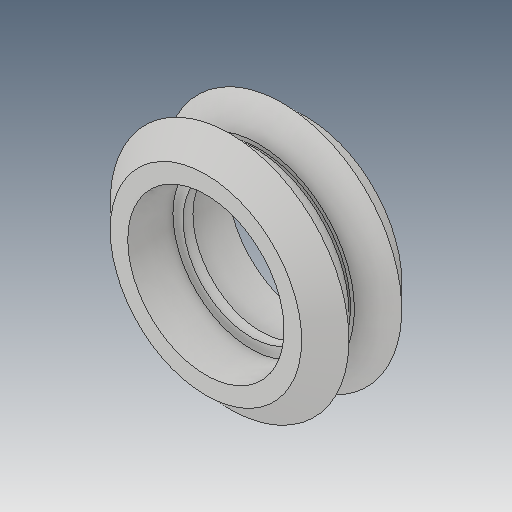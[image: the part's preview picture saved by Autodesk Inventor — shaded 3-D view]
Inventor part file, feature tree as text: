
AUTODESK INVENTOR PART (.ipt)
format: ipt  version: 2017 (Build 210142000, 142)  size: 159,232 bytes
history: native  units: mm
features: sketch x5, other x3
ambient origin geometry x8: Origin, YZ Plane, XZ Plane, XY Plane, X Axis, Y Axis, Z Axis, Center Point
bodies: Solid1 (feature_tree)
feature tree (8):
  other  "dELRIN.ipt"
  other  "Solid1::dELRIN.ipt"
  other  "TaggingFeature1"
  sketch  "Sketch1"  dims[d0=10.0mm]
  sketch  "Sketch2"
  sketch  "Sketch3"
  sketch  "Sketch4"
  sketch  "Sketch5"
